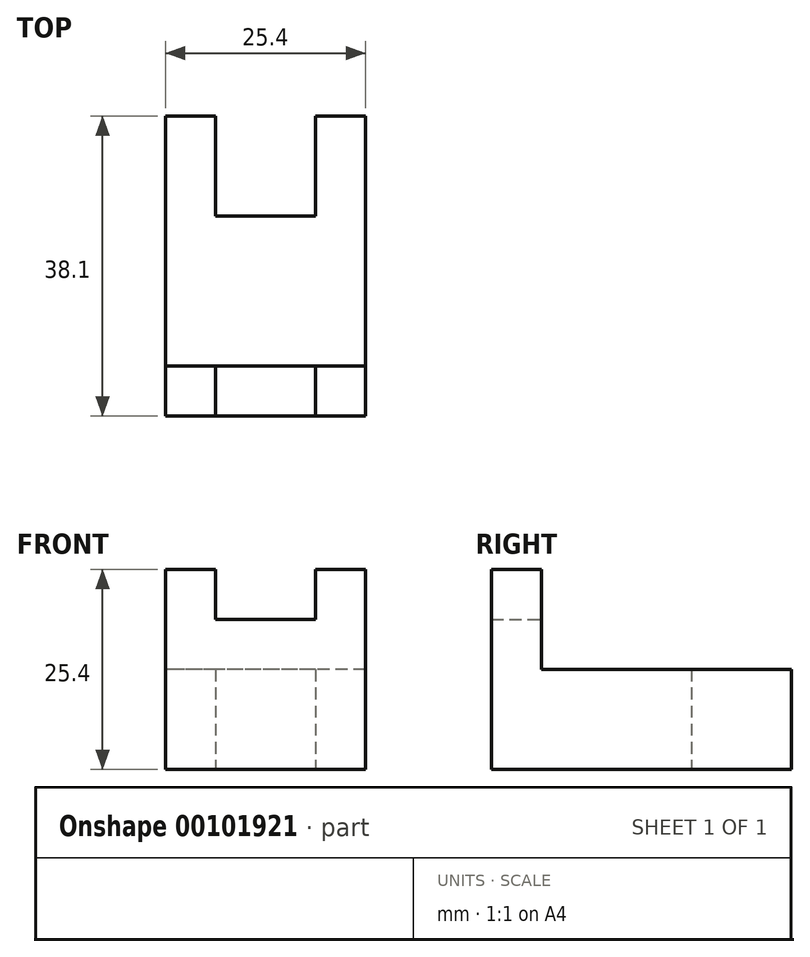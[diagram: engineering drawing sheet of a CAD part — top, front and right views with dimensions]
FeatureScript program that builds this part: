
annotation { "Feature Type Name" : "Feature", "Feature Type Description" : "" }
export const myFeature = defineFeature(function(context is Context, id is Id, definition is map)
    precondition{}
    {
        {
            var Q0;
            Q0=qCreatedBy(makeId("Right.planeOp"),FACE);
            var sketch = newSketch(context, id + "F0", { "sketchPlane" : qUnion([Q0])});
            skLineSegment(sketch, "E0.bottom", {"start": v(0, 0) * mm, "end": v(-38.1, 0) * mm});
            skLineSegment(sketch, "E0.top", {"start": v(-31.75, 25.4) * mm, "end": v(-38.1, 25.4) * mm});
            skLineSegment(sketch, "E0.left", {"start": v(0, 0) * mm, "end": v(0, 12.7) * mm});
            skLineSegment(sketch, "E0.right", {"start": v(-38.1, 0) * mm, "end": v(-38.1, 25.4) * mm});
            skLineSegment(sketch, "E1.top", {"start": v(-31.75, 12.7) * mm, "end": v(0, 12.7) * mm});
            skLineSegment(sketch, "E1.left", {"start": v(-31.75, 25.4) * mm, "end": v(-31.75, 12.7) * mm});
            skSolve(sketch);
        }
        {
            var Q0;
            Q0=makeQuery(id+"F0.imprint","IMPRINT",FACE,{"disambiguationData":[TD([[makeQuery(id+"F0.imprint","IMPRINT",EDGE,{"derivedFrom":sQuery(id+"F0.wireOp",EDGE,"E0.bottom")}),-1.0]])]});
            extrude(context, id + "F1", {"entities" : qUnion([Q0]), "depth" : 25.4 * mm});
        }
        {
            var Q0;
            Q0=qCreatedBy(makeId("Front.planeOp"),FACE);
            var sketch = newSketch(context, id + "F2", { "sketchPlane" : qUnion([Q0])});
            skLineSegment(sketch, "E2.bottom", {"start": v(6.35, 25.4) * mm, "end": v(19.05, 25.4) * mm});
            skLineSegment(sketch, "E2.top", {"start": v(6.35, 19.05) * mm, "end": v(19.05, 19.05) * mm});
            skLineSegment(sketch, "E2.left", {"start": v(6.35, 25.4) * mm, "end": v(6.35, 19.05) * mm});
            skLineSegment(sketch, "E2.right", {"start": v(19.05, 25.4) * mm, "end": v(19.05, 19.05) * mm});
            skSolve(sketch);
        }
        {
            var Q0;
            Q0 = qSketchRegion(id + "F2", true);
            extrude(context, id + "F3", {"entities" : qUnion([Q0]), "operationType" : NewBodyOperationType.REMOVE, "endBound" : BoundingType.THROUGH_ALL, "depth" : 25.4 * mm});
        }
        {
            var Q0;
            Q0=qCreatedBy(makeId("Top.planeOp"),FACE);
            var sketch = newSketch(context, id + "F4", { "sketchPlane" : qUnion([Q0])});
            skLineSegment(sketch, "E3.bottom", {"start": v(6.35, 0) * mm, "end": v(19.05, 0) * mm});
            skLineSegment(sketch, "E3.top", {"start": v(6.35, -12.7) * mm, "end": v(19.05, -12.7) * mm});
            skLineSegment(sketch, "E3.left", {"start": v(6.35, 0) * mm, "end": v(6.35, -12.7) * mm});
            skLineSegment(sketch, "E3.right", {"start": v(19.05, 0) * mm, "end": v(19.05, -12.7) * mm});
            skSolve(sketch);
        }
        {
            var Q0;
            Q0 = qSketchRegion(id + "F4", true);
            extrude(context, id + "F5", {"entities" : qUnion([Q0]), "operationType" : NewBodyOperationType.REMOVE, "endBound" : BoundingType.THROUGH_ALL, "depth" : 25.4 * mm});
        }
    });
